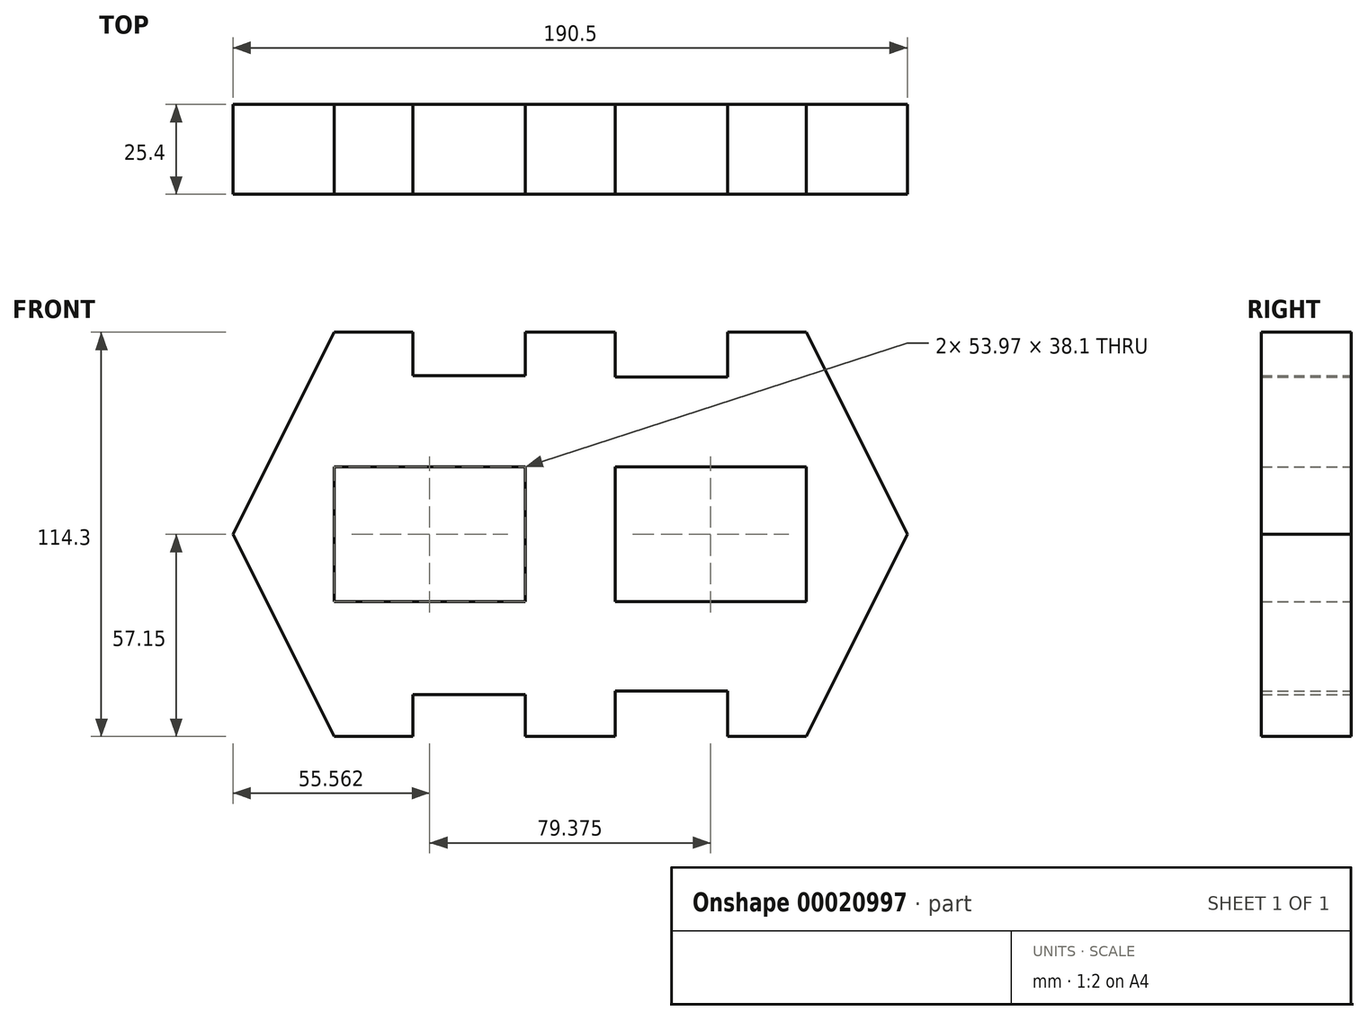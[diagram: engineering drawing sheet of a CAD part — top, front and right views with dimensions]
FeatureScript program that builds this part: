
annotation { "Feature Type Name" : "Feature", "Feature Type Description" : "" }
export const myFeature = defineFeature(function(context is Context, id is Id, definition is map)
    precondition{}
    {
        {
            var Q0;
            Q0=qCreatedBy(makeId("Front.planeOp"),FACE);
            var sketch = newSketch(context, id + "F0", { "sketchPlane" : qUnion([Q0])});
            skLineSegment(sketch, "E0.rect.bottom", {"start": v(66.67, -19.05) * mm, "end": v(12.7, -19.05) * mm});
            skLineSegment(sketch, "E0.rect.top", {"start": v(66.67, 19.05) * mm, "end": v(12.7, 19.05) * mm});
            skLineSegment(sketch, "E0.rect.left", {"start": v(66.67, -19.05) * mm, "end": v(66.67, 19.05) * mm});
            skLineSegment(sketch, "E0.rect.right", {"start": v(-66.68, -19.05) * mm, "end": v(-66.68, 19.05) * mm});
            skPoint(sketch, "E0.rect.middle", {"position": v(0, 0) * mm});
            skLineSegment(sketch, "E1.rect.top", {"start": v(66.67, 57.15) * mm, "end": v(44.45, 57.15) * mm});
            skLineSegment(sketch, "E2.rect.left", {"start": v(12.7, -19.05) * mm, "end": v(12.7, 19.05) * mm});
            skLineSegment(sketch, "E2.rect.right", {"start": v(-12.7, -19.05) * mm, "end": v(-12.7, 19.05) * mm});
            skLineSegment(sketch, "E3.trimOffspring", {"start": v(-12.7, 19.05) * mm, "end": v(-66.68, 19.05) * mm});
            skLineSegment(sketch, "E4.trimOffspring", {"start": v(-12.7, -19.05) * mm, "end": v(-66.68, -19.05) * mm});
            skLineSegment(sketch, "E5.top", {"start": v(-12.7, 44.88) * mm, "end": v(-44.45, 44.88) * mm});
            skLineSegment(sketch, "E5.left", {"start": v(-12.7, 57.15) * mm, "end": v(-12.7, 44.88) * mm});
            skLineSegment(sketch, "E5.right", {"start": v(-44.45, 57.15) * mm, "end": v(-44.45, 44.88) * mm});
            skPoint(sketch, "E6.orphan", {"position": v(-95.25, 57.15) * mm});
            skPoint(sketch, "E7.orphan", {"position": v(-104.1, -57.15) * mm});
            skPoint(sketch, "E8.orphan", {"position": v(104.1, 57.15) * mm});
            skPoint(sketch, "E9.orphan", {"position": v(95.25, -57.15) * mm});
            skLineSegment(sketch, "E10.right", {"start": v(-44.45, -45.32) * mm, "end": v(-44.45, -57.15) * mm});
            skLineSegment(sketch, "E10.left", {"start": v(-12.7, -45.32) * mm, "end": v(-12.7, -57.15) * mm});
            skLineSegment(sketch, "E10.bottom", {"start": v(-12.7, -45.32) * mm, "end": v(-44.45, -45.32) * mm});
            skLineSegment(sketch, "E11.trimOffspring", {"start": v(-44.45, 57.15) * mm, "end": v(-66.67, 57.15) * mm});
            skLineSegment(sketch, "E12", {"start": v(-66.67, -57.15) * mm, "end": v(-44.45, -57.15) * mm});
            skLineSegment(sketch, "E13", {"start": v(-12.7, -57.15) * mm, "end": v(12.7, -57.15) * mm});
            skLineSegment(sketch, "E14.top", {"start": v(44.45, -44.34) * mm, "end": v(12.7, -44.34) * mm});
            skLineSegment(sketch, "E14.left", {"start": v(44.45, -57.15) * mm, "end": v(44.45, -44.34) * mm});
            skLineSegment(sketch, "E14.right", {"start": v(12.7, -57.15) * mm, "end": v(12.7, -44.34) * mm});
            skLineSegment(sketch, "E15.trimOffspring", {"start": v(44.45, -57.15) * mm, "end": v(66.67, -57.15) * mm});
            skLineSegment(sketch, "E16.top", {"start": v(12.7, 44.51) * mm, "end": v(44.45, 44.51) * mm});
            skLineSegment(sketch, "E16.left", {"start": v(12.7, 57.15) * mm, "end": v(12.7, 44.51) * mm});
            skLineSegment(sketch, "E16.right", {"start": v(44.45, 57.15) * mm, "end": v(44.45, 44.51) * mm});
            skLineSegment(sketch, "E17.trimOffspring", {"start": v(12.7, 57.15) * mm, "end": v(-12.7, 57.15) * mm});
            skLineSegment(sketch, "E18.bottom", {"start": v(-66.67, 57.15) * mm, "end": v(-44.45, 57.15) * mm});
            skPoint(sketch, "E19", {"position": v(44.45, -57.15) * mm});
            skPoint(sketch, "E20", {"position": v(-95.25, 0) * mm});
            skPoint(sketch, "E21", {"position": v(95.25, 0) * mm});
            skLineSegment(sketch, "E22", {"start": v(66.67, 57.15) * mm, "end": v(95.25, 0) * mm});
            skLineSegment(sketch, "E23", {"start": v(95.25, 0) * mm, "end": v(66.67, -57.15) * mm});
            skLineSegment(sketch, "E24", {"start": v(-66.67, 57.15) * mm, "end": v(-95.25, 0) * mm});
            skLineSegment(sketch, "E25", {"start": v(-66.67, -57.15) * mm, "end": v(-95.25, 0) * mm});
            skPoint(sketch, "E26.orphan", {"position": v(-95.25, -57.15) * mm});
            skPoint(sketch, "E27.end.orphan", {"position": v(-44.45, -63.02) * mm});
            skPoint(sketch, "E27.start.orphan", {"position": v(-95.25, -63.02) * mm});
            skPoint(sketch, "E28.end.orphan", {"position": v(-66.68, 60.34) * mm});
            skPoint(sketch, "E29.end.orphan", {"position": v(-44.45, 63.32) * mm});
            skPoint(sketch, "E29.start.orphan", {"position": v(-95.25, 63.32) * mm});
            skLineSegment(sketch, "E30.trimOffspring", {"start": v(-12.7, 57.15) * mm, "end": v(12.7, 57.15) * mm});
            skLineSegment(sketch, "E31.trimOffspring", {"start": v(44.45, 57.15) * mm, "end": v(66.67, 57.15) * mm});
            skPoint(sketch, "E32.end.orphan", {"position": v(95.25, 67.2) * mm});
            skPoint(sketch, "E32.start.orphan", {"position": v(44.45, 67.2) * mm});
            skPoint(sketch, "E33.orphan", {"position": v(95.25, 57.15) * mm});
            skSolve(sketch);
        }
        {
            var Q0;
            Q0 = qSketchRegion(id + "F0", true);
            extrude(context, id + "F1", {"entities" : qUnion([Q0]), "depth" : 25.4 * mm});
        }
    });
